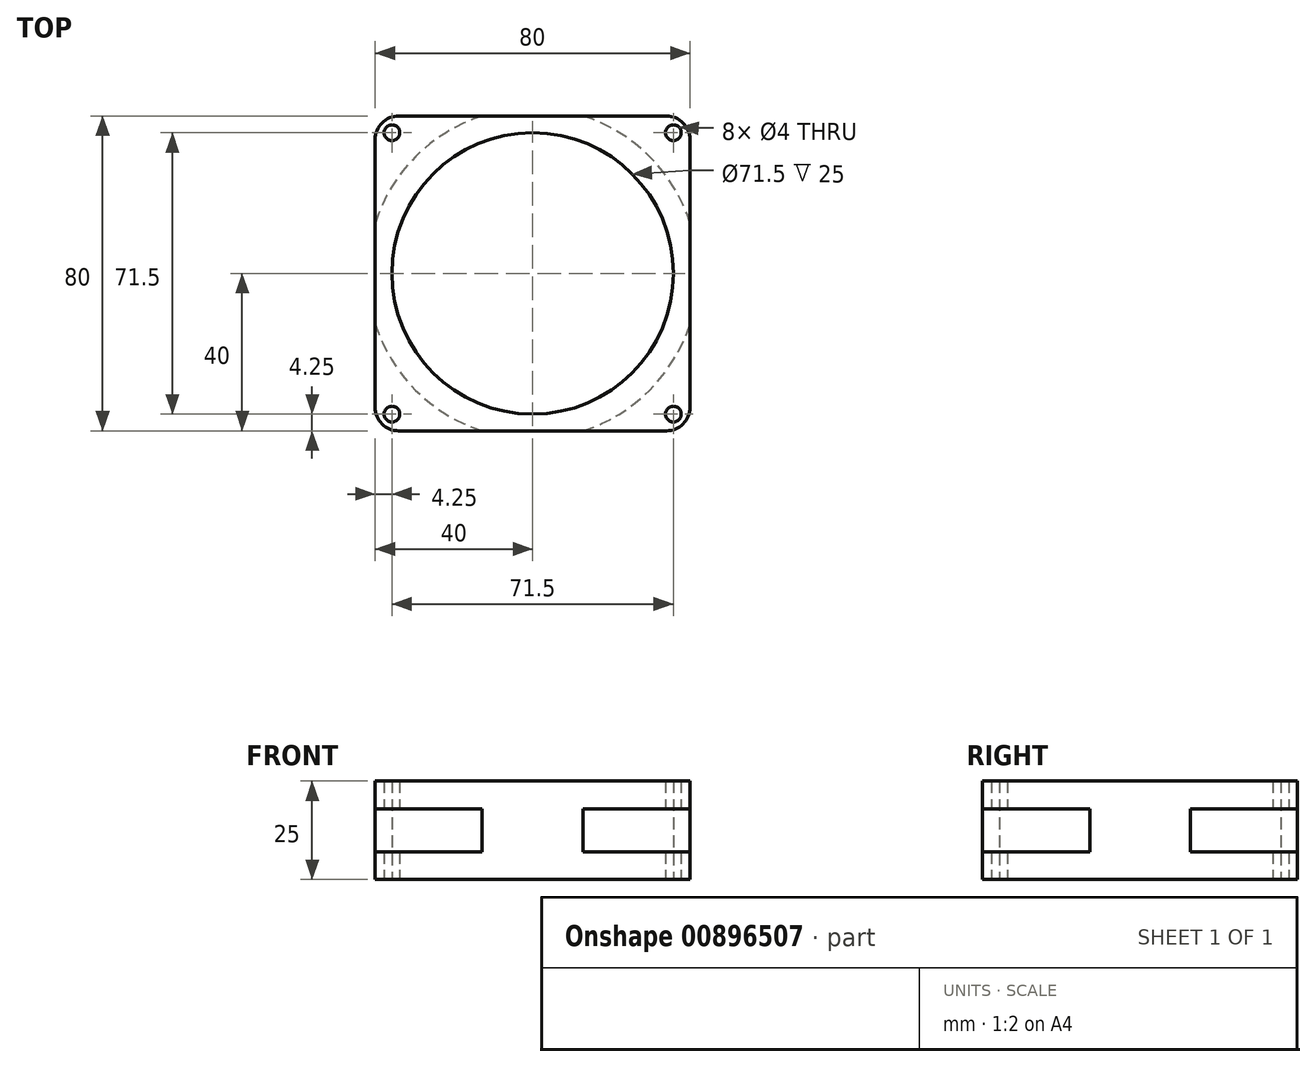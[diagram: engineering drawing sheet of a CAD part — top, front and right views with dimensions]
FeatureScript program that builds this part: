
annotation { "Feature Type Name" : "Feature", "Feature Type Description" : "" }
export const myFeature = defineFeature(function(context is Context, id is Id, definition is map)
    precondition{}
    {
        {
            var Q0;
            Q0=qCreatedBy(makeId("Top.planeOp"),FACE);
            var sketch = newSketch(context, id + "F0", { "sketchPlane" : qUnion([Q0])});
            skLineSegment(sketch, "E0.bottom", {"start": v(40, 40) * mm, "end": v(-40, 40) * mm});
            skLineSegment(sketch, "E0.top", {"start": v(40, -40) * mm, "end": v(-40, -40) * mm});
            skLineSegment(sketch, "E0.left", {"start": v(40, 40) * mm, "end": v(40, -40) * mm});
            skLineSegment(sketch, "E0.right", {"start": v(-40, 40) * mm, "end": v(-40, -40) * mm});
            skPoint(sketch, "E0.middle", {"position": v(0, 0) * mm});
            skLineSegment(sketch, "E1.bottom", {"start": v(35.75, 35.75) * mm, "end": v(-35.75, 35.75) * mm, "construction": true});
            skLineSegment(sketch, "E1.top", {"start": v(35.75, -35.75) * mm, "end": v(-35.75, -35.75) * mm, "construction": true});
            skLineSegment(sketch, "E1.left", {"start": v(35.75, 35.75) * mm, "end": v(35.75, -35.75) * mm, "construction": true});
            skLineSegment(sketch, "E1.right", {"start": v(-35.75, 35.75) * mm, "end": v(-35.75, -35.75) * mm, "construction": true});
            skCircle(sketch, "E2", {"center": v(35.75, 35.75) * mm, "radius": 2 * mm});
            skCircle(sketch, "E3", {"center": v(-35.75, 35.75) * mm, "radius": 2 * mm});
            skCircle(sketch, "E4", {"center": v(-35.75, -35.75) * mm, "radius": 2 * mm});
            skCircle(sketch, "E5", {"center": v(35.75, -35.75) * mm, "radius": 2 * mm});
            skCircle(sketch, "E6", {"center": v(0, 0) * mm, "radius": 35.75 * mm});
            skSolve(sketch);
        }
        {
            var Q0;
            Q0 = qSketchRegion(id + "F0", true);
            extrude(context, id + "F1", {"entities" : qUnion([Q0]), "depth" : 25 * mm, "offsetDistance" : 25 * mm});
        }
        {
            var Q0;
            Q0=makeQuery(id+"F1.opExtrude","SWEPT_EDGE",EDGE,{"disambiguationData":[OSD([sQuery(id+"F0.wireOp",EDGE,"E0.top"),sQuery(id+"F0.wireOp",EDGE,"E0.right")])]});
            var Q1;
            Q1=makeQuery(id+"F1.opExtrude","SWEPT_EDGE",EDGE,{"disambiguationData":[OSD([sQuery(id+"F0.wireOp",EDGE,"E0.top"),sQuery(id+"F0.wireOp",EDGE,"E0.left")])]});
            var Q2;
            Q2=makeQuery(id+"F1.opExtrude","SWEPT_EDGE",EDGE,{"disambiguationData":[OSD([sQuery(id+"F0.wireOp",EDGE,"E0.bottom"),sQuery(id+"F0.wireOp",EDGE,"E0.left")])]});
            var Q3;
            Q3=makeQuery(id+"F1.opExtrude","SWEPT_EDGE",EDGE,{"disambiguationData":[OSD([sQuery(id+"F0.wireOp",EDGE,"E0.bottom"),sQuery(id+"F0.wireOp",EDGE,"E0.right")])]});
            fillet(context, id + "F2", {"entities" : qUnion([Q0, Q1, Q2, Q3]), "tangentPropagation" : true, "radius" : 6 * mm, "defaultsChanged" : true, "vertexSettings" : [], "allowEdgeOverflow" : false});
        }
        {
            var Q0;
            Q0=qCreatedBy(makeId("Top.planeOp"),FACE);
            cPlane(context, id + "F3", {"entities" : qUnion([Q0]), "cplaneType" : CPlaneType.OFFSET, "offset" : 7 * mm, "width" : 150 * mm, "height" : 150 * mm});
        }
        {
            var Q0;
            Q0=qCreatedBy(id+"F3.planeOp",FACE);
            var sketch = newSketch(context, id + "F4", { "sketchPlane" : qUnion([Q0])});
            skCircle(sketch, "E7", {"center": v(0, 0) * mm, "radius": 42 * mm});
            skLineSegment(sketch, "E8.bottom", {"start": v(42, 42) * mm, "end": v(-42, 42) * mm});
            skLineSegment(sketch, "E8.top", {"start": v(42, -42) * mm, "end": v(-42, -42) * mm});
            skLineSegment(sketch, "E8.left", {"start": v(42, 42) * mm, "end": v(42, -42) * mm});
            skLineSegment(sketch, "E8.right", {"start": v(-42, 42) * mm, "end": v(-42, -42) * mm});
            skSolve(sketch);
        }
        {
            var Q0;
            {var subQ0=sQuery(id+"F4.wireOp",EDGE,"E8.bottom");var subQ1=sQuery(id+"F4.wireOp",EDGE,"E7");var subQ2=makeQuery(id+"F4.imprint","INTERSECT",VERTEX,{"derivedFrom":[subQ1,subQ0]});Q0=makeQuery(id+"F4.imprint","IMPRINT",FACE,{"disambiguationData":[TD([[makeQuery(id+"F4.imprint","IMPRINT",EDGE,{"disambiguationData":[TD([[subQ2,1.0]])],"derivedFrom":subQ1}),-1.0]])]});}
            var Q1;
            {var subQ0=sQuery(id+"F4.wireOp",EDGE,"E8.bottom");var subQ1=sQuery(id+"F4.wireOp",EDGE,"E7");var subQ2=makeQuery(id+"F4.imprint","INTERSECT",VERTEX,{"derivedFrom":[subQ1,subQ0]});Q1=makeQuery(id+"F4.imprint","IMPRINT",FACE,{"disambiguationData":[TD([[makeQuery(id+"F4.imprint","IMPRINT",EDGE,{"disambiguationData":[TD([[subQ2,-1.0]])],"derivedFrom":subQ1}),-1.0]])]});}
            var Q2;
            {var subQ0=sQuery(id+"F4.wireOp",EDGE,"E8.right");var subQ1=sQuery(id+"F4.wireOp",EDGE,"E7");var subQ2=makeQuery(id+"F4.imprint","INTERSECT",VERTEX,{"derivedFrom":[subQ1,subQ0]});Q2=makeQuery(id+"F4.imprint","IMPRINT",FACE,{"disambiguationData":[TD([[makeQuery(id+"F4.imprint","IMPRINT",EDGE,{"disambiguationData":[TD([[subQ2,-1.0]])],"derivedFrom":subQ1}),-1.0]])]});}
            var Q3;
            {var subQ0=sQuery(id+"F4.wireOp",EDGE,"E8.left");var subQ1=sQuery(id+"F4.wireOp",EDGE,"E7");var subQ2=makeQuery(id+"F4.imprint","INTERSECT",VERTEX,{"derivedFrom":[subQ1,subQ0]});Q3=makeQuery(id+"F4.imprint","IMPRINT",FACE,{"disambiguationData":[TD([[makeQuery(id+"F4.imprint","IMPRINT",EDGE,{"disambiguationData":[TD([[subQ2,1.0]])],"derivedFrom":subQ1}),-1.0]])]});}
            extrude(context, id + "F5", {"entities" : qUnion([Q0, Q1, Q2, Q3]), "operationType" : NewBodyOperationType.REMOVE, "depth" : 11 * mm, "offsetDistance" : 25 * mm});
        }
    });
